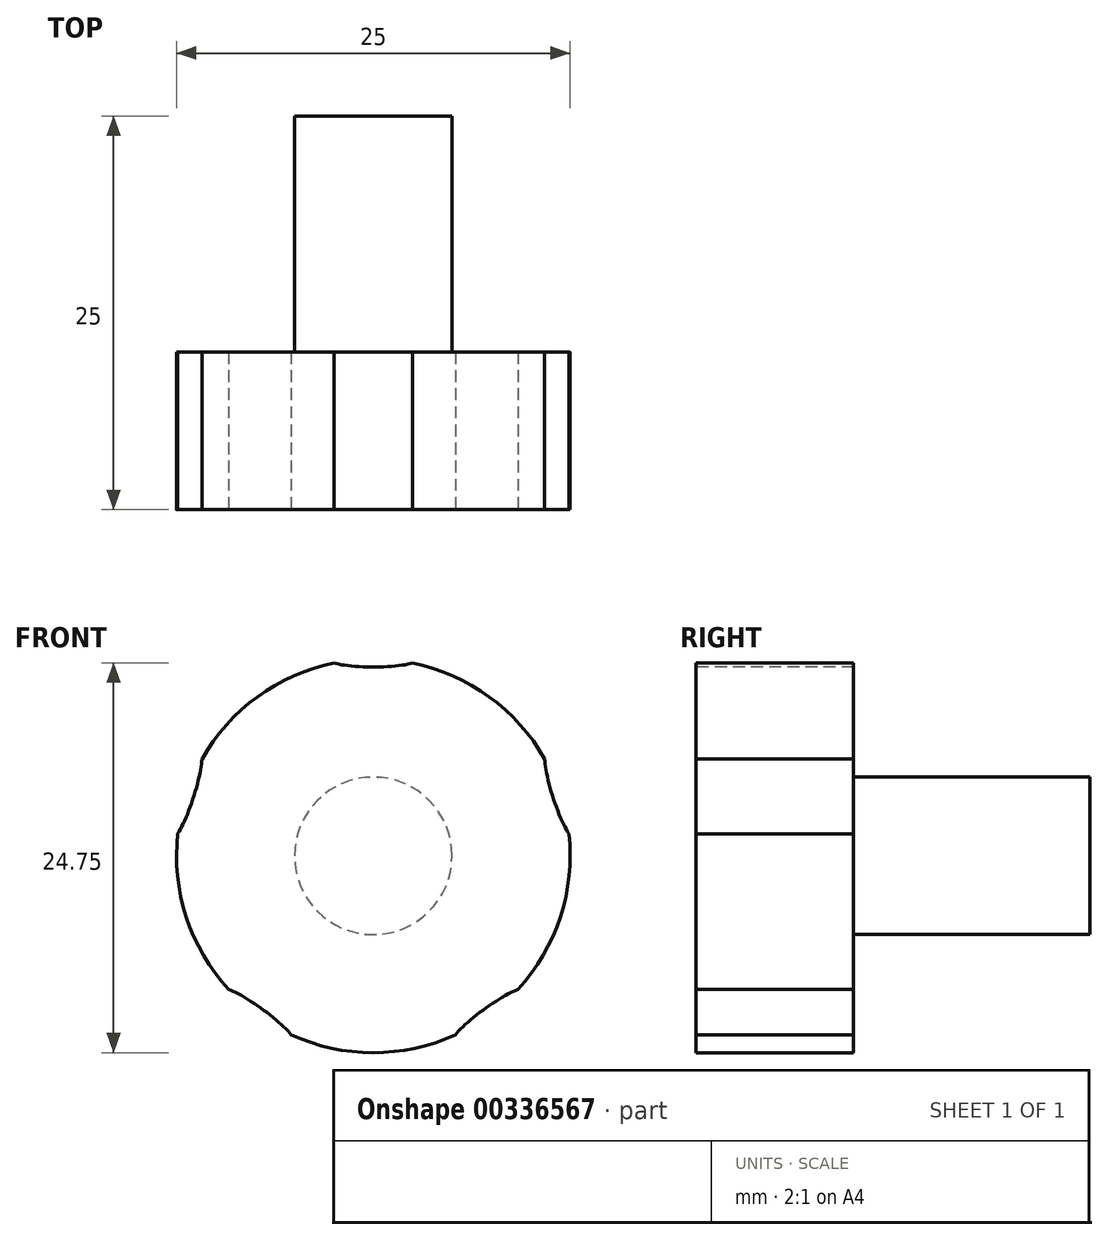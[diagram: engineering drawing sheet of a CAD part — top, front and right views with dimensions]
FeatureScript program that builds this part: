
annotation { "Feature Type Name" : "Feature", "Feature Type Description" : "" }
export const myFeature = defineFeature(function(context is Context, id is Id, definition is map)
    precondition{}
    {
        {
            var Q0;
            Q0=qCreatedBy(makeId("Front.planeOp"),FACE);
            var sketch = newSketch(context, id + "F0", { "sketchPlane" : qUnion([Q0])});
            skCircle(sketch, "E0", {"center": v(0, 0) * mm, "radius": 5 * mm});
            skCircle(sketch, "E1", {"center": v(0, 0) * mm, "radius": 12.5 * mm});
            skEllipticalArc(sketch, "E2", {});
            skEllipticalArc(sketch, "E3.1.0", {});
            skEllipticalArc(sketch, "E3.2.0", {});
            skEllipticalArc(sketch, "E3.3.0", {});
            skEllipticalArc(sketch, "E3.4.0", {});
            skPoint(sketch, "E3.center", {"position": v(0, -0.01) * mm});
            const initialGuessF0  = {"E2": [0, 0.0125, -1, 0, 0.0028966722670498955, 0.0005, 0.5295008083710386, 2.612091845218759], "E3.1.0": [-0.011902324734856654, 0.0038578766098717214, -0.30901699437494756, -0.9510565162951536, 0.0028966722670498955, 0.0005, 0.5295008083710366, 2.612091845218757], "E3.2.0": [-0.007361197585688391, -0.01013246988330956, 0.8090169943749476, -0.587785252292473, 0.0028966722670498955, 0.0005, 0.5295008083710384, 2.612091845218759], "E3.3.0": [0.00734769807458917, -0.010136856140355213, 0.8090169943749473, 0.5877852522924732, 0.0028966722670498955, 0.0005, 0.5295008083710382, 2.612091845218758], "E3.4.0": [0.011897168380448263, 0.0038507794968884648, -0.3090169943749475, 0.9510565162951536, 0.0028966722670498955, 0.0005, 0.5295008083710387, 2.612091845218759]};
            skSetInitialGuess(sketch, initialGuessF0);
            skSolve(sketch);
        }
        {
            var Q0;
            Q0=makeQuery(id+"F0.imprint","IMPRINT",FACE,{"disambiguationData":[TD([[makeQuery(id+"F0.imprint","IMPRINT",EDGE,{"derivedFrom":sQuery(id+"F0.wireOp",EDGE,"E0")}),1.0]])]});
            extrude(context, id + "F1", {"entities" : qUnion([Q0]), "oppositeDirection" : true, "depth" : 25 * mm});
        }
        {
            var Q0;
            Q0=makeQuery(id+"F0.imprint","IMPRINT",FACE,{"disambiguationData":[TD([[makeQuery(id+"F0.imprint","IMPRINT",EDGE,{"derivedFrom":sQuery(id+"F0.wireOp",EDGE,"E0")}),-1.0]])]});
            extrude(context, id + "F2", {"entities" : qUnion([Q0]), "operationType" : NewBodyOperationType.ADD, "oppositeDirection" : true, "depth" : 10 * mm});
        }
    });
